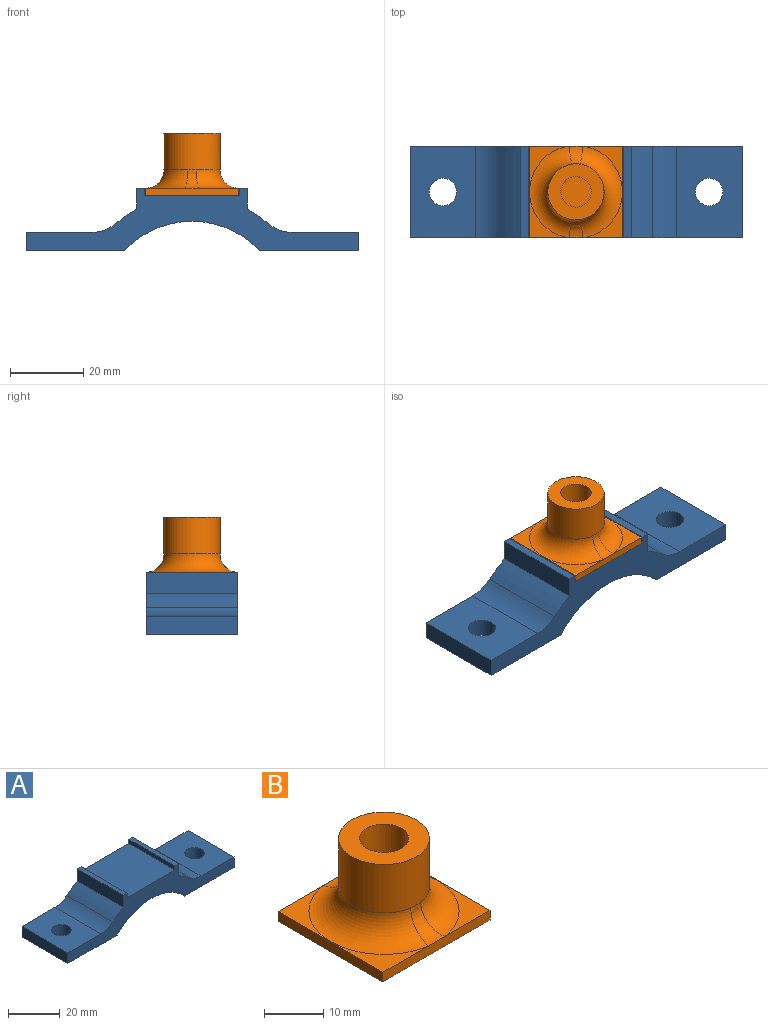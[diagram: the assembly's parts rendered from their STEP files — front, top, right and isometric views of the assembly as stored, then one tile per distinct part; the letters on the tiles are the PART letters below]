
ASSEMBLY  parts=2 mates=1
PART A: 22 faces, bbox 90.5x25x17 mm
  f0: plane 26x25mm, normal (0,0,1), area 650mm2, adj f10,f11,f19,f21
  f1: cylinder r=32.25mm len=25mm, axis (0,1,0), area 176.2mm2, adj f10,f11,f13,f17
  f2: cylinder r=32.25mm len=25mm, axis (0,1,0), area 176.2mm2, adj f10,f11,f12,f16
  f3: plane 25x17.96mm, normal (0,0,1), area 404.7mm2, adj f4,f10,f11,f12,f14
  f4: plane 25x5mm, normal (-1,0,0), area 125mm2, adj f3,f5,f10,f11
  f5: plane 26.81x25mm, normal (0,0,-1), area 626.1mm2, adj f4,f6,f10,f11,f14
  f6: cylinder r=25.25mm len=36.88mm, axis (0,1,0), area 1033.6mm2, adj f5,f7,f10,f11
  f7: plane 26.81x25mm, normal (0,0,-1), area 626.1mm2, adj f6,f8,f10,f11,f15
  f8: plane 25x5mm, normal (1,0,0), area 125mm2, adj f7,f9,f10,f11
  f9: plane 25x17.96mm, normal (0,0,1), area 404.7mm2, adj f8,f10,f11,f13,f15
  f10: plane 90.5x17mm, normal (0,-1,0), area 618.6mm2, adj f0,f1,f2,f3,f4,f5,f6,f7
  f11: plane 90.5x17mm, normal (0,1,0), area 618.6mm2, adj f0,f1,f2,f3,f4,f5,f6,f7
  f12: cylinder r=10mm len=25mm, axis (0,1,0), area 175.6mm2, adj f2,f3,f10,f11
  f13: cylinder r=10mm len=25mm, axis (0,1,0), area 175.6mm2, adj f1,f9,f10,f11
  f14: cylinder r=3.75mm len=7.5mm, axis (0,0,1), area 117.8mm2, adj f3,f5
  f15: cylinder r=3.75mm len=7.5mm, axis (0,0,1), area 117.8mm2, adj f7,f9
  f16: plane 25x5.7mm, normal (-1,0,0), area 142.5mm2, adj f2,f10,f11,f18
  f17: plane 25x5.7mm, normal (1,0,0), area 142.5mm2, adj f1,f10,f11,f20
  f18: plane 25x2mm, normal (0,0,1), area 50mm2, adj f10,f11,f16,f19
  f19: plane 25x2mm, normal (1,0,0), area 50mm2, adj f0,f10,f11,f18
  f20: plane 25x2mm, normal (0,0,1), area 50mm2, adj f10,f11,f17,f21
  f21: plane 25x2mm, normal (-1,0,0), area 50mm2, adj f0,f10,f11,f20
PART B: 15 faces, bbox 35.1x34.7x17 mm
  f0: plane 25x10.81mm, normal (0,0,1), area 67.8mm2, adj f2,f5,f6,f12
  f1: plane 25x10.81mm, normal (0,0,1), area 67.8mm2, adj f4,f5,f6,f13
  f2: plane 25x2mm, normal (-1,0,0), area 50mm2, adj f0,f3,f5,f6
  f3: plane 25.5x25mm, normal (0,0,-1), area 637.5mm2, adj f2,f4,f5,f6
  f4: plane 25x2mm, normal (1,0,0), area 50mm2, adj f1,f3,f5,f6
  f5: plane 25.51x2.01mm, normal (0,-1,0), area 51mm2, adj f0,f1,f2,f3,f4,f14
  f6: plane 25.51x2.01mm, normal (0,1,0), area 51mm2, adj f0,f1,f2,f3,f4,f11
  f7: cylinder r=4.15mm len=15mm, axis (0,0,-1), area 391.1mm2, adj f9,f10
  f8: cylinder r=7.65mm len=15.3mm, axis (0,0,-1), area 480.7mm2, adj f9,f11,f12,f13,f14
  f9: plane 15.3x15.3mm, normal (0,0,1), area 129.7mm2, adj f7,f8
  f10: plane 8.3x8.3mm, normal (0,0,1), area 54.1mm2, adj f7
  f11: bspline ~5.44x5.19mm, area 22.5mm2, adj f6,f8,f12,f13
  f12: torus R=12.65mm, axis (0,0,1), area 210.7mm2, adj f0,f8,f11,f14
  f13: torus R=12.65mm, axis (0,0,1), area 210.7mm2, adj f1,f8,f11,f14
  f14: bspline ~5.44x5.19mm, area 22.5mm2, adj f5,f8,f12,f13
PLACE A t=(0,0,-4)mm
PLACE B t=(-12.75,0,28.25)mm
MATE planar B.f7 <-> A.f0  axis (0,0,-1) through (0,-12.5,28.25)mm
